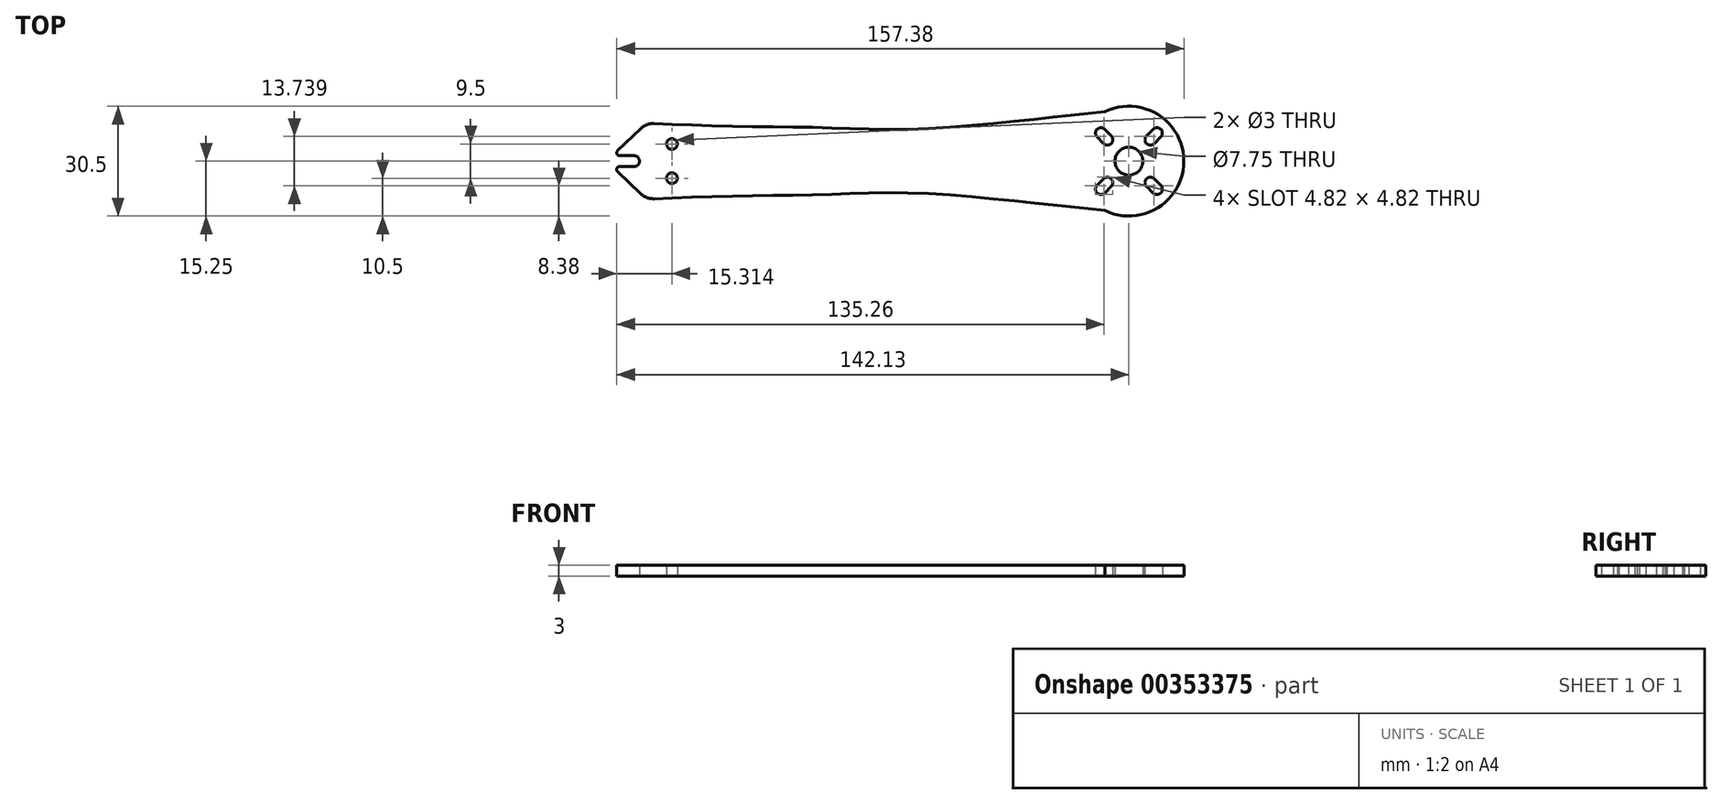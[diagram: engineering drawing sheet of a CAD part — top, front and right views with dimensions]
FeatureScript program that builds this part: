
annotation { "Feature Type Name" : "Feature", "Feature Type Description" : "" }
export const myFeature = defineFeature(function(context is Context, id is Id, definition is map)
    precondition{}
    {
        {
            var Q0;
            Q0=qCreatedBy(makeId("Top.planeOp"),FACE);
            var sketch = newSketch(context, id + "F0", { "sketchPlane" : qUnion([Q0])});
            skArc(sketch, "E0", {"start": v(-6.68, -13.7) * mm, "mid": v(15.25, 0) * mm, "end": v(-6.68, 13.7) * mm});
            skLineSegment(sketch, "E1", {"start": v(41.94, 0) * mm, "end": v(15.25, 0) * mm});
            skCircle(sketch, "E2", {"center": v(0, 0) * mm, "radius": 3.88 * mm});
            skFitSpline(sketch, "E3", {"points": [v(-6.68, 13.7) * mm, v(-28.75, 11.37) * mm, v(-59.97, 8.84) * mm, v(-85.21, 9.3) * mm, v(-112.76, 9.76) * mm, v(-136.63, 10.68) * mm, v(-146.73, 11.14) * mm], "startDerivative": vector(-126.66, -13.55) * mm, "endDerivative": vector(-81.3, 3.65) * mm});
            skFitSpline(sketch, "E4.MirrorCS", {"points": [v(-6.68, -13.7) * mm, v(-28.75, -11.37) * mm, v(-59.97, -8.84) * mm, v(-85.21, -9.3) * mm, v(-112.76, -9.76) * mm, v(-136.63, -10.68) * mm, v(-146.73, -11.14) * mm], "startDerivative": vector(-126.66, 13.55) * mm, "endDerivative": vector(-81.3, -3.65) * mm});
            skLineSegment(sketch, "E5", {"start": v(-141.88, 2.89) * mm, "end": v(-135.44, 9.07) * mm});
            skLineSegment(sketch, "E6.MirrorCS", {"start": v(-141.88, -2.89) * mm, "end": v(-135.44, -9.07) * mm});
            skPoint(sketch, "E7.1.internal.orphan", {"position": v(-156.6, 0) * mm});
            skCircle(sketch, "E8", {"center": v(-126.82, 4.75) * mm, "radius": 1.5 * mm});
            skArc(sketch, "E9", {"start": v(-137.32, -1.5) * mm, "mid": v(-135.82, 0) * mm, "end": v(-137.32, 1.5) * mm});
            skCircle(sketch, "E10.MirrorC", {"center": v(-126.82, -4.75) * mm, "radius": 1.5 * mm});
            skArc(sketch, "E11", {"start": v(-6.72, 8.84) * mm, "mid": v(-8.84, 8.84) * mm, "end": v(-8.84, 6.72) * mm});
            skLineSegment(sketch, "E12", {"start": v(-137.32, 1.5) * mm, "end": v(-141.32, 1.5) * mm});
            skLineSegment(sketch, "E13", {"start": v(-137.32, -1.5) * mm, "end": v(-141.32, -1.5) * mm});
            skPoint(sketch, "E14.start.orphan", {"position": v(-146.73, 0) * mm});
            skPoint(sketch, "E15.visualSharp", {"position": v(-133.89, 10.55) * mm});
            skArc(sketch, "E15.filletArc", {"start": v(-131.75, 10.46) * mm, "mid": v(-133.74, 10.14) * mm, "end": v(-135.44, 9.07) * mm});
            skPoint(sketch, "E16.visualSharp", {"position": v(-133.89, -10.55) * mm});
            skArc(sketch, "E16.filletArc", {"start": v(-135.44, -9.07) * mm, "mid": v(-133.74, -10.14) * mm, "end": v(-131.75, -10.46) * mm});
            skPoint(sketch, "E17.visualSharp", {"position": v(-143.33, -1.5) * mm});
            skArc(sketch, "E17.filletArc", {"start": v(-141.32, -1.5) * mm, "mid": v(-142.07, -2) * mm, "end": v(-141.88, -2.89) * mm});
            skPoint(sketch, "E18.visualSharp", {"position": v(-143.33, 1.5) * mm});
            skArc(sketch, "E18.filletArc", {"start": v(-141.88, 2.89) * mm, "mid": v(-142.07, 2) * mm, "end": v(-141.32, 1.5) * mm});
            skArc(sketch, "E19", {"start": v(-7.02, 4.9) * mm, "mid": v(-4.9, 4.9) * mm, "end": v(-4.9, 7.02) * mm});
            skArc(sketch, "E20.MirrorC", {"start": v(7.02, 4.9) * mm, "mid": v(4.9, 4.9) * mm, "end": v(4.9, 7.02) * mm});
            skArc(sketch, "E21.MirrorC", {"start": v(-7.02, -4.9) * mm, "mid": v(-4.9, -4.9) * mm, "end": v(-4.9, -7.02) * mm});
            skArc(sketch, "E22.MirrorC", {"start": v(-6.72, -8.84) * mm, "mid": v(-8.84, -8.84) * mm, "end": v(-8.84, -6.72) * mm});
            skArc(sketch, "E23.MirrorC", {"start": v(7.02, -4.9) * mm, "mid": v(4.9, -4.9) * mm, "end": v(4.9, -7.02) * mm});
            skArc(sketch, "E24.MirrorC", {"start": v(6.72, -8.84) * mm, "mid": v(8.84, -8.84) * mm, "end": v(8.84, -6.72) * mm});
            skLineSegment(sketch, "E25.trimOffspring", {"start": v(0, 0) * mm, "end": v(-3.88, 0) * mm});
            skPoint(sketch, "E26.trimOffspring.end.orphan", {"position": v(-39.36, -39.36) * mm});
            skPoint(sketch, "E27.trimOffspring.end.orphan", {"position": v(39.36, -39.36) * mm});
            skPoint(sketch, "E28.trimOffspring.end.orphan", {"position": v(39.36, 39.36) * mm});
            skPoint(sketch, "E29.trimOffspring.end.orphan", {"position": v(-39.36, 39.36) * mm});
            skLineSegment(sketch, "E30", {"start": v(-6.72, 8.84) * mm, "end": v(-4.9, 7.02) * mm});
            skLineSegment(sketch, "E31", {"start": v(-8.84, 6.72) * mm, "end": v(-7.02, 4.9) * mm});
            skLineSegment(sketch, "E32.MirrorCS", {"start": v(6.72, 8.84) * mm, "end": v(4.9, 7.02) * mm});
            skLineSegment(sketch, "E33.MirrorCS", {"start": v(8.84, 6.72) * mm, "end": v(7.02, 4.9) * mm});
            skLineSegment(sketch, "E34.trimOffspring", {"start": v(7.02, -4.9) * mm, "end": v(8.84, -6.72) * mm});
            skLineSegment(sketch, "E35.trimOffspring", {"start": v(-4.9, -7.02) * mm, "end": v(-6.72, -8.84) * mm});
            skLineSegment(sketch, "E36.trimOffspring", {"start": v(4.9, -7.02) * mm, "end": v(6.72, -8.84) * mm});
            skLineSegment(sketch, "E37.trimOffspring", {"start": v(-7.02, -4.9) * mm, "end": v(-8.84, -6.72) * mm});
            skPoint(sketch, "E38.orphan", {"position": v(10.58, -8.46) * mm});
            skPoint(sketch, "E39.orphan", {"position": v(8, -10.11) * mm});
            skPoint(sketch, "E40.orphan", {"position": v(-8, -10.11) * mm});
            skPoint(sketch, "E41.orphan", {"position": v(-10.58, -8.46) * mm});
            skArc(sketch, "E42.trimOffspring", {"start": v(6.72, 8.84) * mm, "mid": v(8.84, 8.84) * mm, "end": v(8.84, 6.72) * mm});
            skSolve(sketch);
        }
        {
            var Q0;
            Q0=makeQuery(id+"F0.imprint","IMPRINT",FACE,{"disambiguationData":[TD([[makeQuery(id+"F0.imprint","IMPRINT",EDGE,{"derivedFrom":sQuery(id+"F0.wireOp",EDGE,"E2")}),-1.0]])]});
            extrude(context, id + "F1", {"entities" : qUnion([Q0]), "depth" : 3 * mm});
        }
    });
